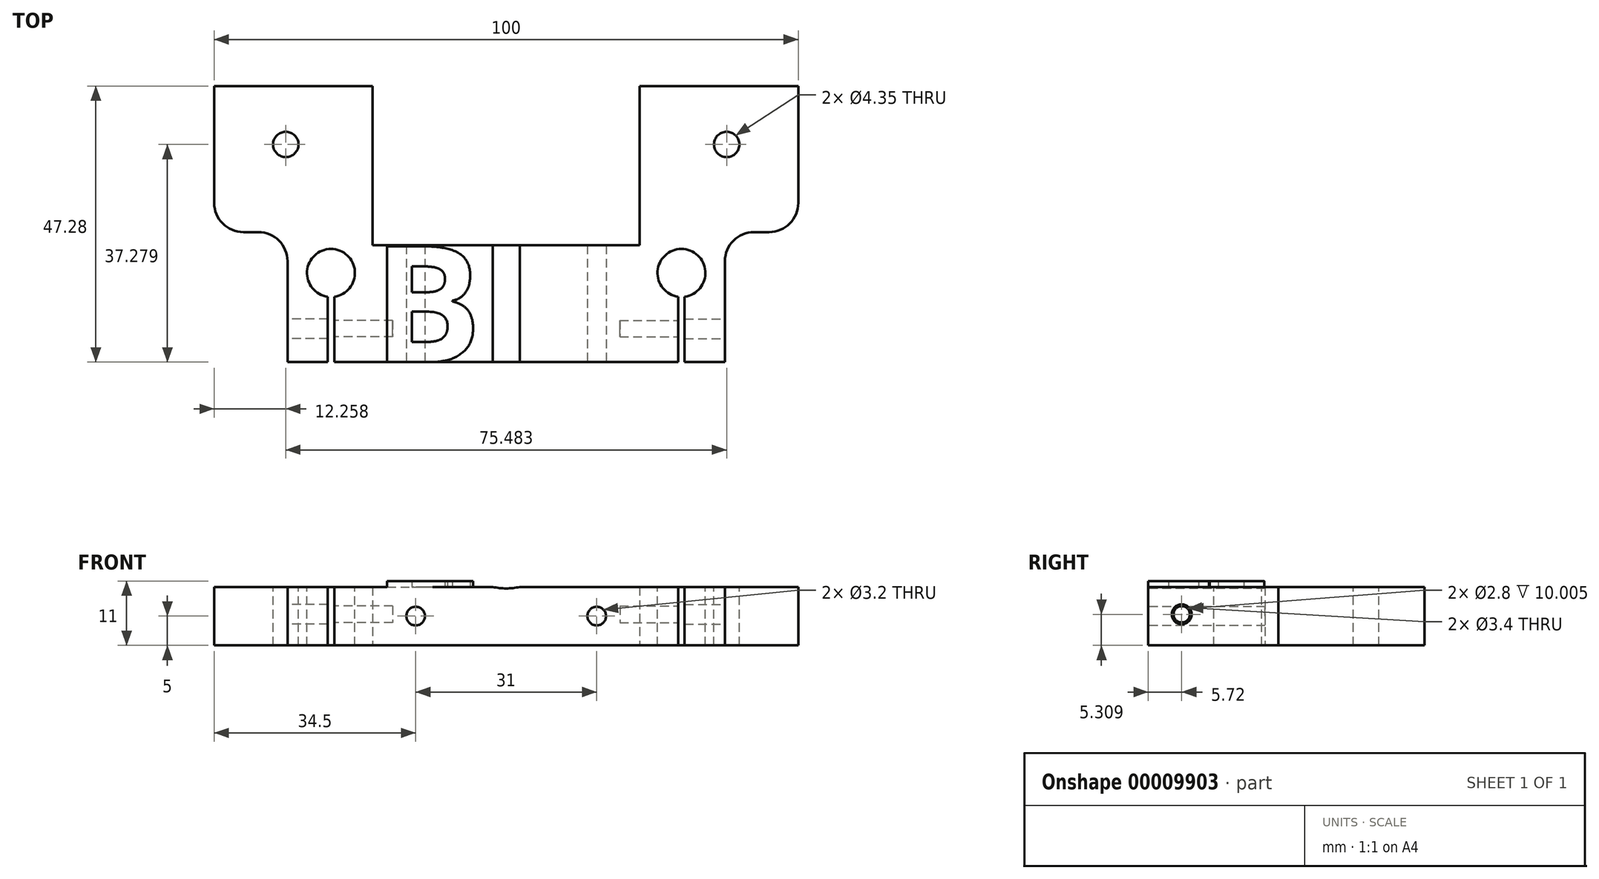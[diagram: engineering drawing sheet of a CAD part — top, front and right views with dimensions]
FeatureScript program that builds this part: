
annotation { "Feature Type Name" : "Feature", "Feature Type Description" : "" }
export const myFeature = defineFeature(function(context is Context, id is Id, definition is map)
    precondition{}
    {
        {
            var Q0;
            Q0=qCreatedBy(makeId("Top.planeOp"),FACE);
            var sketch = newSketch(context, id + "F0", { "sketchPlane" : qUnion([Q0])});
            skLineSegment(sketch, "E0", {"start": v(0, -13.82) * mm, "end": v(-37.44, -13.82) * mm});
            skLineSegment(sketch, "E1", {"start": v(-37.44, -13.82) * mm, "end": v(-37.44, 8.46) * mm});
            skLineSegment(sketch, "E2", {"start": v(-37.44, 8.46) * mm, "end": v(-50, 8.46) * mm});
            skLineSegment(sketch, "E3", {"start": v(-50, 8.46) * mm, "end": v(-50, 33.46) * mm});
            skLineSegment(sketch, "E4", {"start": v(-50, 33.46) * mm, "end": v(-22.87, 33.46) * mm});
            skLineSegment(sketch, "E5", {"start": v(-22.87, 33.46) * mm, "end": v(-22.87, 6.18) * mm});
            skLineSegment(sketch, "E6", {"start": v(-22.87, 6.18) * mm, "end": v(0, 6.18) * mm});
            skLineSegment(sketch, "E7", {"start": v(0, 6.18) * mm, "end": v(0, -13.82) * mm});
            skSolve(sketch);
        }
        {
            var Q0;
            Q0=qSketchRegion(id+"F0",true);
            extrude(context, id + "F1", {"entities" : qUnion([Q0]), "depth" : 10 * mm});
        }
        {
            var Q0;
            Q0=makeQuery(id+"F1.opExtrude","SWEPT_FACE",FACE,{"disambiguationData":[OSD([sQuery(id+"F0.wireOp",EDGE,"E0")])]});
            var sketch = newSketch(context, id + "F2", { "sketchPlane" : qUnion([Q0])});
            skLineSegment(sketch, "E8", {"start": v(0, 5) * mm, "end": v(0, 5) * mm});
            skCircle(sketch, "E9", {"center": v(-15.5, 5) * mm, "radius": 1.6 * mm});
            skCircle(sketch, "E10", {"center": v(0, 20.5) * mm, "radius": 10.75 * mm});
            skSolve(sketch);
        }
        {
            var Q0;
            Q0=qSketchRegion(id+"F2",true);
            extrude(context, id + "F3", {"entities" : qUnion([Q0]), "operationType" : NewBodyOperationType.REMOVE, "endBound" : BoundingType.THROUGH_ALL, "oppositeDirection" : true, "depth" : 25 * mm});
        }
        {
            var Q0;
            {var subQ0=makeQuery(id+"F1.opExtrude","CAP_FACE",FACE,{"disambiguationData":[OSD([sQuery(id+"F0.wireOp",EDGE,"E0"),sQuery(id+"F0.wireOp",EDGE,"fd64a43a-5635-4f94-a977-4dd36923accb"),sQuery(id+"F0.wireOp",EDGE,"1334f7d4-4c90-4769-8fa3-fe5f576fb005"),sQuery(id+"F0.wireOp",EDGE,"E1"),sQuery(id+"F0.wireOp",EDGE,"E2"),sQuery(id+"F0.wireOp",EDGE,"E3"),sQuery(id+"F0.wireOp",EDGE,"E4"),sQuery(id+"F0.wireOp",EDGE,"E5"),sQuery(id+"F0.wireOp",EDGE,"E6"),sQuery(id+"F0.wireOp",EDGE,"E7")])],"isStart":false});Q0=makeQuery(id+"F11.boolean.opBoolean","MERGE",FACE,{"derivedFrom":[subQ0,makeQuery(id+"F11.opPattern","COPY",FACE,{"derivedFrom":subQ0,"instanceName":"1"})]});}
            var sketch = newSketch(context, id + "F4", { "sketchPlane" : qUnion([Q0])});
            skCircle(sketch, "E11", {"center": v(-30, 1.46) * mm, "radius": 4.1 * mm});
            skCircle(sketch, "E12", {"center": v(-37.74, 23.46) * mm, "radius": 2.17 * mm});
            skLineSegment(sketch, "E13", {"start": v(-30, 1.46) * mm, "end": v(-30, -13.82) * mm, "construction": true});
            skLineSegment(sketch, "E14.bottom", {"start": v(-30.55, -1.63) * mm, "end": v(-29.45, -1.63) * mm});
            skLineSegment(sketch, "E14.top", {"start": v(-30.55, -14.74) * mm, "end": v(-29.45, -14.74) * mm});
            skLineSegment(sketch, "E14.left", {"start": v(-30.55, -1.63) * mm, "end": v(-30.55, -14.74) * mm});
            skLineSegment(sketch, "E14.right", {"start": v(-29.45, -1.63) * mm, "end": v(-29.45, -14.74) * mm});
            skPoint(sketch, "E15", {"position": v(-30, -1.63) * mm});
            skSolve(sketch);
        }
        {
            var Q0;
            Q0=qSketchRegion(id+"F4",true);
            var Q1;
            {var subQ3=sQuery(id+"F4.wireOp",EDGE,"E14.bottom");Q1=makeQuery(id+"F4.imprint","IMPRINT",FACE,{"disambiguationData":[TD([[makeQuery(id+"F4.imprint","IMPRINT",EDGE,{"derivedFrom":subQ3}),-1.0]])]});}
            extrude(context, id + "F5", {"entities" : qUnion([Q0, Q1]), "operationType" : NewBodyOperationType.REMOVE, "endBound" : BoundingType.THROUGH_ALL, "oppositeDirection" : true, "depth" : 25 * mm});
        }
        {
            var Q0;
            Q0=makeQuery(id+"F1.opExtrude","SWEPT_EDGE",EDGE,{"disambiguationData":[OSD([sQuery(id+"F0.wireOp",EDGE,"E2"),sQuery(id+"F0.wireOp",EDGE,"E3")])]});
            fillet(context, id + "F6", {"entities" : qUnion([Q0]), "radius" : 5 * mm, "tangentPropagation" : true, "allowEdgeOverflow" : false});
        }
        {
            var Q0;
            Q0=makeQuery(id+"F1.opExtrude","SWEPT_EDGE",EDGE,{"disambiguationData":[OSD([sQuery(id+"F0.wireOp",EDGE,"E1"),sQuery(id+"F0.wireOp",EDGE,"E2")])]});
            fillet(context, id + "F7", {"entities" : qUnion([Q0]), "radius" : 5 * mm, "tangentPropagation" : true, "allowEdgeOverflow" : false});
        }
        {
            var Q0;
            Q0=makeQuery(id+"F1.opExtrude","SWEPT_FACE",FACE,{"disambiguationData":[OSD([sQuery(id+"F0.wireOp",EDGE,"E1")])]});
            var sketch = newSketch(context, id + "F8", { "sketchPlane" : qUnion([Q0])});
            skCircle(sketch, "E16", {"center": v(8.1, 5.3) * mm, "radius": 1.7 * mm});
            skCircle(sketch, "E17", {"center": v(8.1, 5.3) * mm, "radius": 1.4 * mm});
            skSolve(sketch);
        }
        {
            var Q0;
            Q0=makeQuery(id+"F8.imprint","IMPRINT",FACE,{"disambiguationData":[TD([[makeQuery(id+"F8.imprint","IMPRINT",EDGE,{"derivedFrom":sQuery(id+"F8.wireOp",EDGE,"E17")}),1.0]])]});
            extrude(context, id + "F9", {"entities" : qUnion([Q0]), "operationType" : NewBodyOperationType.REMOVE, "oppositeDirection" : true, "depth" : 18 * mm});
        }
        {
            var Q0;
            Q0=makeQuery(id+"F8.imprint","IMPRINT",FACE,{"disambiguationData":[TD([[makeQuery(id+"F8.imprint","IMPRINT",EDGE,{"derivedFrom":sQuery(id+"F8.wireOp",EDGE,"E17")}),1.0]])]});
            var Q1;
            Q1=makeQuery(id+"F8.imprint","IMPRINT",FACE,{"disambiguationData":[TD([[makeQuery(id+"F8.imprint","IMPRINT",EDGE,{"derivedFrom":sQuery(id+"F8.wireOp",EDGE,"E16")}),1.0]])]});
            extrude(context, id + "F10", {"entities" : qUnion([Q0, Q1]), "operationType" : NewBodyOperationType.REMOVE, "endBound" : BoundingType.UP_TO_NEXT, "oppositeDirection" : true, "depth" : 25 * mm});
        }
        {
            var Q0;
            Q0=makeQuery(id+"F1.opExtrude","SWEPT_BODY",BODY,{"disambiguationData":[OSD([sQuery(id+"F0.wireOp",EDGE,"E0"),sQuery(id+"F0.wireOp",EDGE,"fd64a43a-5635-4f94-a977-4dd36923accb"),sQuery(id+"F0.wireOp",EDGE,"1334f7d4-4c90-4769-8fa3-fe5f576fb005"),sQuery(id+"F0.wireOp",EDGE,"E1"),sQuery(id+"F0.wireOp",EDGE,"E2"),sQuery(id+"F0.wireOp",EDGE,"E3"),sQuery(id+"F0.wireOp",EDGE,"E4"),sQuery(id+"F0.wireOp",EDGE,"E5"),sQuery(id+"F0.wireOp",EDGE,"E6"),sQuery(id+"F0.wireOp",EDGE,"E7")])]});
            var Q1;
            Q1=qCreatedBy(makeId("Right.planeOp"),FACE);
            mirror(context, id + "F11", {"operationType" : NewBodyOperationType.ADD, "entities" : qUnion([Q0]), "mirrorPlane" : qUnion([Q1])});
        }
        {
            var Q0;
            Q0=makeQuery(id+"F1.opExtrude","CAP_FACE",FACE,{"disambiguationData":[OSD([sQuery(id+"F0.wireOp",EDGE,"E0"),sQuery(id+"F0.wireOp",EDGE,"E1"),sQuery(id+"F0.wireOp",EDGE,"E2"),sQuery(id+"F0.wireOp",EDGE,"E3"),sQuery(id+"F0.wireOp",EDGE,"E4"),sQuery(id+"F0.wireOp",EDGE,"E5"),sQuery(id+"F0.wireOp",EDGE,"E6"),sQuery(id+"F0.wireOp",EDGE,"E7")])],"isStart":false});
            var sketch = newSketch(context, id + "F12", { "sketchPlane" : qUnion([Q0])});
            skText(sketch, "E18", { "text": "B", "fontName": "OpenSans-Bold.ttf"});
            const initialGuessF12  = {"E18": [-0.02287, -0.01382, 1, 0, 0.02]};
            skSetInitialGuess(sketch, initialGuessF12);
            skSolve(sketch);
        }
        {
            var Q0;
            Q0 = qSketchRegion(id + "F12", true);
            extrude(context, id + "F13", {"entities" : qUnion([Q0]), "operationType" : NewBodyOperationType.ADD, "depth" : 1 * mm});
        }
    });
